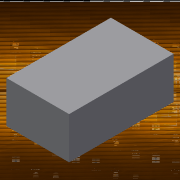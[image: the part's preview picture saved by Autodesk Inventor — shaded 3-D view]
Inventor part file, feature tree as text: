
AUTODESK INVENTOR PART (.ipt)
format: ipt  version: 2017 (Build 210142000, 142)  size: 95,232 bytes
history: native  units: in
note: dims shown in document units (in); Inventor stores cm internally (conversion verified against a paired STEP export)
features: extrude x1, sketch x1
ambient origin geometry x8: Origin, YZ Plane, XZ Plane, XY Plane, X Axis, Y Axis, Z Axis, Center Point
bodies: Solid1 (feature_tree)
feature tree (2):
  extrude  "Extrusion1"  Depth=0.1in
  sketch  "Sketch1"  dims[d0=0.15in d1=0.1in d2=0.25in d3=0.0in]
